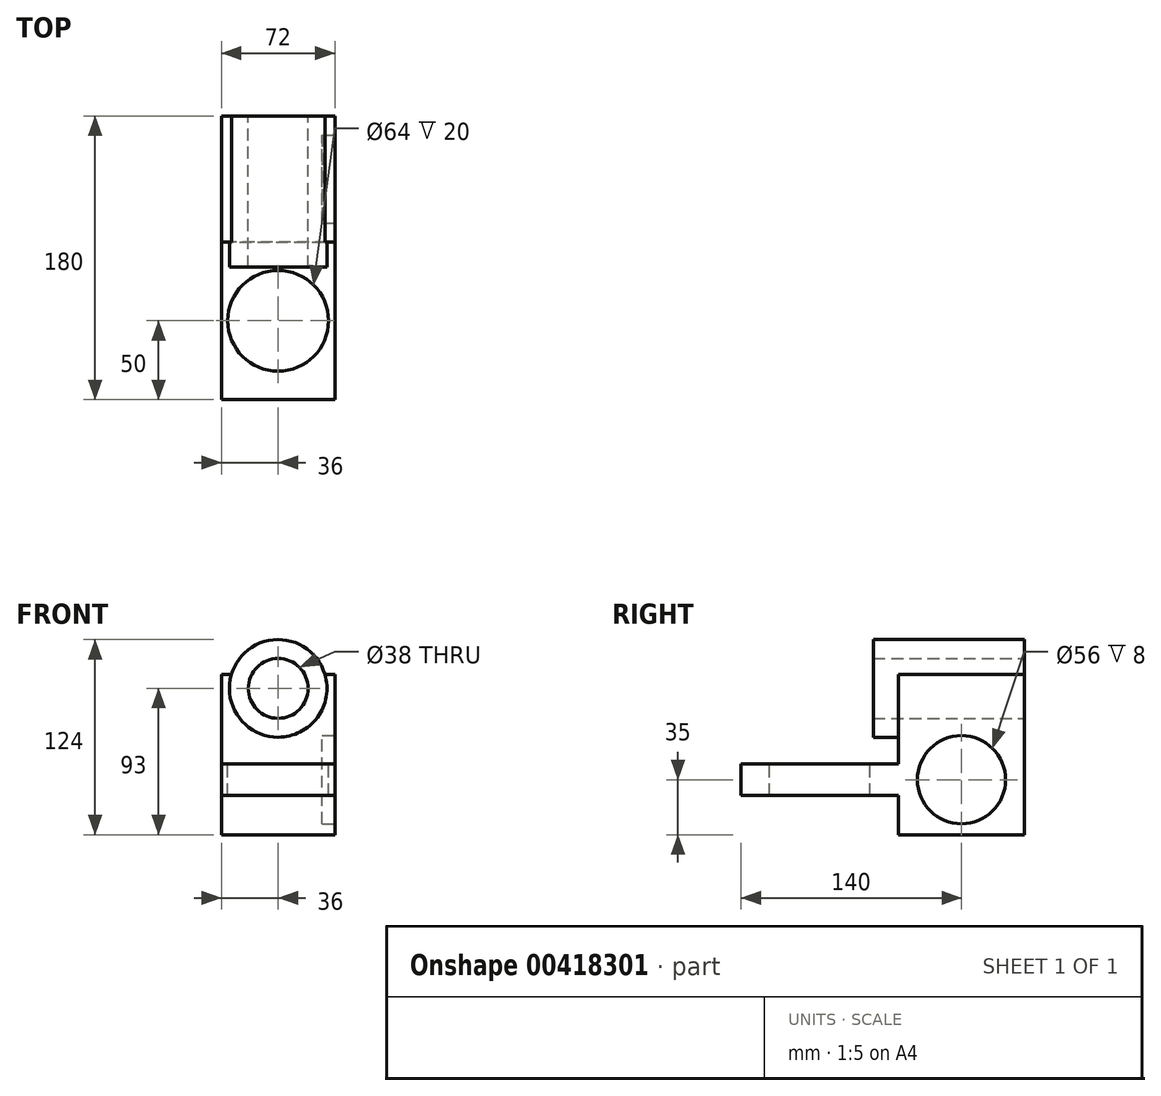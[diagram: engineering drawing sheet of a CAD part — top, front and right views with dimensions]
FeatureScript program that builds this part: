
annotation { "Feature Type Name" : "Feature", "Feature Type Description" : "" }
export const myFeature = defineFeature(function(context is Context, id is Id, definition is map)
    precondition{}
    {
        {
            var Q0;
            Q0=qCreatedBy(makeId("Right.planeOp"),FACE);
            var sketch = newSketch(context, id + "F0", { "sketchPlane" : qUnion([Q0])});
            skLineSegment(sketch, "E0.bottom", {"start": v(-40, 51) * mm, "end": v(40, 51) * mm});
            skLineSegment(sketch, "E0.top", {"start": v(-40, -51) * mm, "end": v(40, -51) * mm});
            skLineSegment(sketch, "E0.left", {"start": v(-40, 51) * mm, "end": v(-40, -51) * mm});
            skLineSegment(sketch, "E0.right", {"start": v(40, 51) * mm, "end": v(40, -51) * mm});
            skPoint(sketch, "E0.middle", {"position": v(0, 0) * mm});
            skSolve(sketch);
        }
        {
            var Q0;
            Q0 = qSketchRegion(id + "F0", true);
            extrude(context, id + "F1", {"entities" : qUnion([Q0]), "endBound" : BoundingType.SYMMETRIC, "depth" : 72 * mm});
        }
        {
            var Q0;
            Q0=makeQuery(id+"F1.opExtrude","CAP_FACE",FACE,{"disambiguationData":[OSD([sQuery(id+"F0.wireOp",EDGE,"E0.bottom"),sQuery(id+"F0.wireOp",EDGE,"E0.top"),sQuery(id+"F0.wireOp",EDGE,"E0.left"),sQuery(id+"F0.wireOp",EDGE,"E0.right")])],"isStart":false});
            var sketch = newSketch(context, id + "F2", { "sketchPlane" : qUnion([Q0])});
            skLineSegment(sketch, "E1.bottom", {"start": v(-40, -6) * mm, "end": v(-140, -6) * mm});
            skLineSegment(sketch, "E1.top", {"start": v(-40, -26) * mm, "end": v(-140, -26) * mm});
            skLineSegment(sketch, "E1.left", {"start": v(-40, -6) * mm, "end": v(-40, -26) * mm});
            skLineSegment(sketch, "E1.right", {"start": v(-140, -6) * mm, "end": v(-140, -26) * mm});
            skSolve(sketch);
        }
        {
            var Q0;
            Q0 = qSketchRegion(id + "F2", true);
            var Q1;
            Q1=makeQuery(id+"F1.opExtrude","CAP_FACE",FACE,{"disambiguationData":[OSD([sQuery(id+"F0.wireOp",EDGE,"E0.bottom"),sQuery(id+"F0.wireOp",EDGE,"E0.top"),sQuery(id+"F0.wireOp",EDGE,"E0.left"),sQuery(id+"F0.wireOp",EDGE,"E0.right")])],"isStart":true});
            extrude(context, id + "F3", {"entities" : qUnion([Q0]), "operationType" : NewBodyOperationType.ADD, "endBound" : BoundingType.UP_TO_SURFACE, "oppositeDirection" : true, "endBoundEntityFace" : qUnion([Q1]), "depth" : (2 * 96) * mm});
        }
        {
            var Q0;
            Q0=makeQuery(id+"F3.boolean.opBoolean","MERGE",FACE,{"derivedFrom":[makeQuery(id+"F1.opExtrude","CAP_FACE",FACE,{"disambiguationData":[OSD([sQuery(id+"F0.wireOp",EDGE,"E0.bottom"),sQuery(id+"F0.wireOp",EDGE,"E0.top"),sQuery(id+"F0.wireOp",EDGE,"E0.left"),sQuery(id+"F0.wireOp",EDGE,"E0.right")])],"isStart":false}),makeQuery(id+"F3.opExtrude","CAP_FACE",FACE,{"disambiguationData":[OSD([sQuery(id+"F2.wireOp",EDGE,"E1.bottom"),sQuery(id+"F2.wireOp",EDGE,"E1.top"),sQuery(id+"F2.wireOp",EDGE,"E1.left"),sQuery(id+"F2.wireOp",EDGE,"E1.right")])],"isStart":true})]});
            var sketch = newSketch(context, id + "F4", { "sketchPlane" : qUnion([Q0])});
            skCircle(sketch, "E2", {"center": v(0, -16) * mm, "radius": 28 * mm});
            skSolve(sketch);
        }
        {
            var Q0;
            Q0 = qSketchRegion(id + "F4", true);
            extrude(context, id + "F5", {"entities" : qUnion([Q0]), "operationType" : NewBodyOperationType.REMOVE, "oppositeDirection" : true, "depth" : 8 * mm});
        }
        {
            var Q0;
            {var subQ1=sQuery(id+"F0.wireOp",EDGE,"E0.left");var subQ3=sQuery(id+"F0.wireOp",EDGE,"E0.bottom");Q0=makeQuery(id+"F3.boolean.opBoolean","SPLIT",FACE,{"disambiguationData":[TD([makeQuery(id+"F1.opExtrude","SWEPT_FACE",FACE,{"disambiguationData":[OSD([subQ3])]})])],"derivedFrom":makeQuery(id+"F1.opExtrude","SWEPT_FACE",FACE,{"disambiguationData":[OSD([subQ1])]})});}
            var sketch = newSketch(context, id + "F6", { "sketchPlane" : qUnion([Q0])});
            skCircle(sketch, "E3", {"center": v(0, 42) * mm, "radius": 31 * mm});
            skLineSegment(sketch, "E4", {"start": v(0, 51) * mm, "end": v(0, -6) * mm, "construction": true});
            skCircle(sketch, "E5", {"center": v(0, 42) * mm, "radius": 19 * mm});
            skSolve(sketch);
        }
        {
            var Q0;
            Q0 = qSketchRegion(id + "F6", true);
            extrude(context, id + "F7", {"entities" : qUnion([Q0]), "operationType" : NewBodyOperationType.ADD, "depth" : 16 * mm, "hasSecondDirection" : true, "secondDirectionOppositeDirection" : true, "secondDirectionDepth" : (96 - 16) * mm});
        }
        {
            var Q0;
            {var subQ0=sQuery(id+"F0.wireOp",EDGE,"E0.bottom");var subQ1=makeQuery(id+"F1.opExtrude","SWEPT_FACE",FACE,{"disambiguationData":[OSD([subQ0])]});var subQ3=sQuery(id+"F0.wireOp",EDGE,"E0.left");Q0=makeQuery(id+"F7.boolean.opBoolean","SPLIT",FACE,{"disambiguationData":[TD([makeQuery(id+"F7.opExtrude","SWEPT_FACE",FACE,{"disambiguationData":[OSD([sQuery(id+"F6.wireOp",EDGE,"E5")])]})])],"derivedFrom":makeQuery(id+"F3.boolean.opBoolean","SPLIT",FACE,{"disambiguationData":[TD([subQ1])],"derivedFrom":makeQuery(id+"F1.opExtrude","SWEPT_FACE",FACE,{"disambiguationData":[OSD([subQ3])]})})});}
            extrude(context, id + "F8", {"entities" : qUnion([Q0]), "operationType" : NewBodyOperationType.REMOVE, "endBound" : BoundingType.THROUGH_ALL, "oppositeDirection" : true, "depth" : 25 * mm});
        }
        {
            var Q0;
            Q0=makeQuery(id+"F3.opExtrude","SWEPT_FACE",FACE,{"disambiguationData":[OSD([sQuery(id+"F2.wireOp",EDGE,"E1.bottom")])]});
            var sketch = newSketch(context, id + "F9", { "sketchPlane" : qUnion([Q0])});
            skCircle(sketch, "E6", {"center": v(0, -90) * mm, "radius": 32 * mm});
            skPoint(sketch, "E6.centerSnap0", {"position": v(-36, -90) * mm});
            skPoint(sketch, "E6.centerSnap1", {"position": v(0, -140) * mm});
            skSolve(sketch);
        }
        {
            var Q0;
            Q0 = qSketchRegion(id + "F9", true);
            extrude(context, id + "F10", {"entities" : qUnion([Q0]), "operationType" : NewBodyOperationType.REMOVE, "endBound" : BoundingType.THROUGH_ALL, "oppositeDirection" : true, "depth" : 25 * mm});
        }
    });
